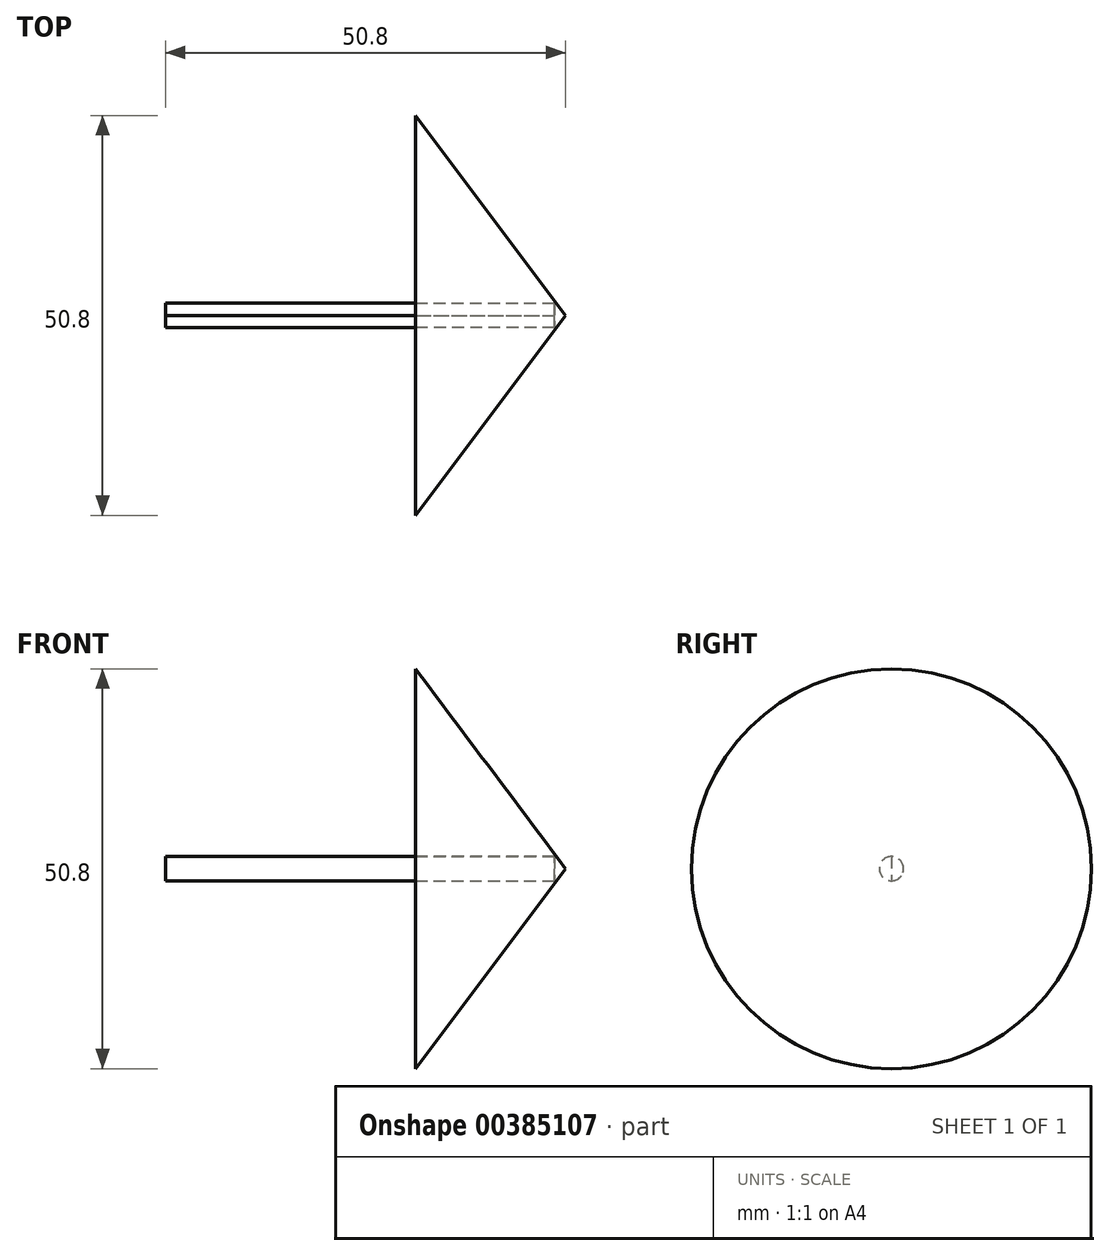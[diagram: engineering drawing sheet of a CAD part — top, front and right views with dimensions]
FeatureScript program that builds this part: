
annotation { "Feature Type Name" : "Feature", "Feature Type Description" : "" }
export const myFeature = defineFeature(function(context is Context, id is Id, definition is map)
    precondition{}
    {
        {
            var Q0;
            Q0=qCreatedBy(makeId("Front.planeOp"),FACE);
            var sketch = newSketch(context, id + "F0", { "sketchPlane" : qUnion([Q0])});
            skLineSegment(sketch, "E0.bottom", {"start": v(0, 0) * mm, "end": v(49.4, 0) * mm});
            skLineSegment(sketch, "E0.top", {"start": v(0, 1.54) * mm, "end": v(49.4, 1.54) * mm});
            skLineSegment(sketch, "E0.left", {"start": v(0, 0) * mm, "end": v(0, 1.54) * mm});
            skLineSegment(sketch, "E0.right", {"start": v(49.4, 0) * mm, "end": v(49.4, 1.54) * mm});
            skSolve(sketch);
        }
        {
            var Q0;
            Q0=makeQuery(id+"F0.imprint","IMPRINT",FACE,{"disambiguationData":[TD([[makeQuery(id+"F0.imprint","IMPRINT",EDGE,{"derivedFrom":sQuery(id+"F0.wireOp",EDGE,"E0.bottom")}),1.0]])]});
            var Q1;
            Q1=sQuery(id+"F0.wireOp",EDGE,"E0.bottom");
            revolve(context, id + "F1", {"entities" : qUnion([Q0]), "axis" : qUnion([Q1]), "revolveType" : RevolveType.FULL});
        }
        {
            var Q0;
            Q0=qCreatedBy(makeId("Front.planeOp"),FACE);
            var sketch = newSketch(context, id + "F2", { "sketchPlane" : qUnion([Q0])});
            skLineSegment(sketch, "E1", {"start": v(31.75, 0) * mm, "end": v(31.75, 25.4) * mm});
            skLineSegment(sketch, "E2", {"start": v(31.75, 25.4) * mm, "end": v(50.8, 0) * mm});
            skLineSegment(sketch, "E3", {"start": v(50.8, 0) * mm, "end": v(31.75, 0) * mm});
            skLineSegment(sketch, "E4", {"start": v(49.41, 1.59) * mm, "end": v(49.4, 1.59) * mm});
            skSolve(sketch);
        }
        {
            var Q0;
            Q0=makeQuery(id+"F2.imprint","IMPRINT",FACE,{"disambiguationData":[TD([[makeQuery(id+"F2.imprint","IMPRINT",EDGE,{"derivedFrom":sQuery(id+"F2.wireOp",EDGE,"E1")}),-1.0]])]});
            var Q1;
            Q1=sQuery(id+"F2.wireOp",EDGE,"E3");
            revolve(context, id + "F3", {"entities" : qUnion([Q0]), "axis" : qUnion([Q1]), "revolveType" : RevolveType.FULL, "oppositeDirection" : true});
        }
        {
            var Q0;
            Q0=makeQuery(id+"F0.imprint","IMPRINT",FACE,{"disambiguationData":[TD([[makeQuery(id+"F0.imprint","IMPRINT",EDGE,{"derivedFrom":sQuery(id+"F0.wireOp",EDGE,"E0.bottom")}),1.0]])]});
            var Q1;
            Q1=sQuery(id+"F2.wireOp",EDGE,"E3");
            revolve(context, id + "F4", {"entities" : qUnion([Q0]), "axis" : qUnion([Q1]), "revolveType" : RevolveType.ONE_DIRECTION, "angle" : 180 * degree});
        }
    });
